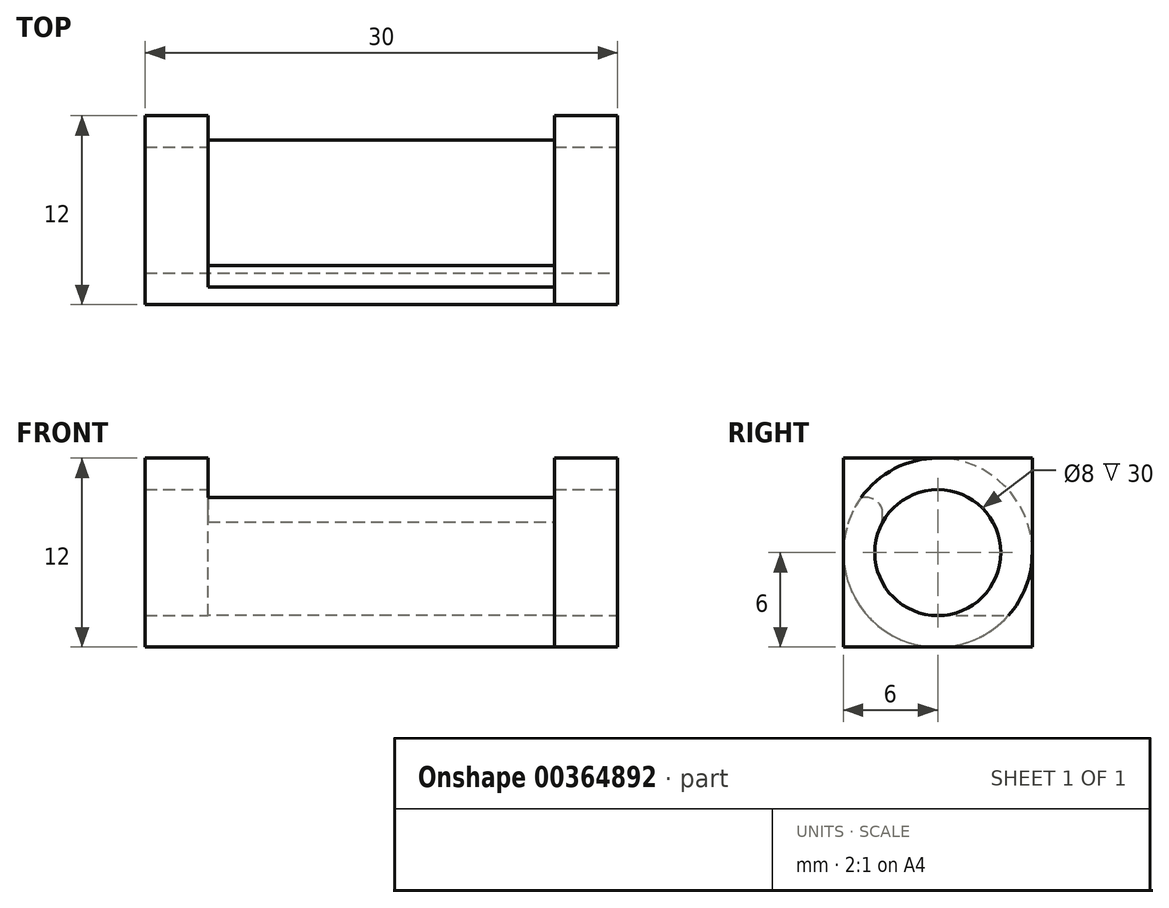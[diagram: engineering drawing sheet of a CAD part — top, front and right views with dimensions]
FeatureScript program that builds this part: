
annotation { "Feature Type Name" : "Feature", "Feature Type Description" : "" }
export const myFeature = defineFeature(function(context is Context, id is Id, definition is map)
    precondition{}
    {
        {
            var Q0;
            Q0=qCreatedBy(makeId("Right.planeOp"),FACE);
            var sketch = newSketch(context, id + "F0", { "sketchPlane" : qUnion([Q0])});
            skCircle(sketch, "E0", {"center": v(0, 0) * mm, "radius": 6 * mm});
            skSolve(sketch);
        }
        {
            var Q0;
            Q0 = qSketchRegion(id + "F0", true);
            extrude(context, id + "F1", {"entities" : qUnion([Q0]), "depth" : 30 * mm});
        }
        {
            var Q0;
            Q0=makeQuery(id+"F1.opExtrude","CAP_FACE",FACE,{"disambiguationData":[OSD([sQuery(id+"F0.wireOp",EDGE,"E0")])],"isStart":false});
            var sketch = newSketch(context, id + "F2", { "sketchPlane" : qUnion([Q0])});
            skCircle(sketch, "E1", {"center": v(0, 0) * mm, "radius": 4 * mm});
            skSolve(sketch);
        }
        {
            var Q0;
            Q0 = qSketchRegion(id + "F2", true);
            extrude(context, id + "F3", {"entities" : qUnion([Q0]), "operationType" : NewBodyOperationType.REMOVE, "endBound" : BoundingType.THROUGH_ALL, "oppositeDirection" : true, "depth" : 25 * mm});
        }
        {
            var Q0;
            Q0=makeQuery(id+"F1.opExtrude","CAP_FACE",FACE,{"disambiguationData":[OSD([sQuery(id+"F0.wireOp",EDGE,"E0")])],"isStart":false});
            cPlane(context, id + "F4", {"entities" : qUnion([Q0]), "cplaneType" : CPlaneType.OFFSET, "offset" : 4 * mm, "oppositeDirection" : true, "width" : 150 * mm, "height" : 150 * mm});
        }
        {
            var Q0;
            Q0=qCreatedBy(id+"F4.planeOp",FACE);
            var sketch = newSketch(context, id + "F5", { "sketchPlane" : qUnion([Q0])});
            skLineSegment(sketch, "E2", {"start": v(0, -4) * mm, "end": v(8, -4) * mm});
            skLineSegment(sketch, "E3", {"start": v(-4.5, 3.5) * mm, "end": v(-7.72, 3.5) * mm});
            skLineSegment(sketch, "E4", {"start": v(-7.72, 3.5) * mm, "end": v(-7.72, 9.46) * mm});
            skLineSegment(sketch, "E5", {"start": v(-7.72, 9.46) * mm, "end": v(8.98, 9.46) * mm});
            skLineSegment(sketch, "E6", {"start": v(8.98, 9.46) * mm, "end": v(8, -4) * mm});
            skLineSegment(sketch, "E7", {"start": v(0, -4) * mm, "end": v(0, 0) * mm});
            skLineSegment(sketch, "E8", {"start": v(0, 0) * mm, "end": v(-3.5, 0) * mm});
            skLineSegment(sketch, "E9", {"start": v(-3.5, 0) * mm, "end": v(-3.5, 2.5) * mm});
            skPoint(sketch, "E10.visualSharp", {"position": v(-3.5, 3.5) * mm});
            skArc(sketch, "E10.filletArc", {"start": v(-3.5, 2.5) * mm, "mid": v(-3.8, 3.2) * mm, "end": v(-4.5, 3.5) * mm});
            skSolve(sketch);
        }
        {
            var Q0;
            Q0 = qSketchRegion(id + "F5", true);
            extrude(context, id + "F6", {"entities" : qUnion([Q0]), "operationType" : NewBodyOperationType.REMOVE, "oppositeDirection" : true, "depth" : 22 * mm});
        }
        {
            var Q0;
            Q0=makeQuery(id+"F1.opExtrude","CAP_FACE",FACE,{"disambiguationData":[OSD([sQuery(id+"F0.wireOp",EDGE,"E0")])],"isStart":false});
            var sketch = newSketch(context, id + "F7", { "sketchPlane" : qUnion([Q0])});
            skLineSegment(sketch, "E11.bottom", {"start": v(6, -6) * mm, "end": v(-6, -6) * mm});
            skLineSegment(sketch, "E11.top", {"start": v(6, 6) * mm, "end": v(-6, 6) * mm});
            skLineSegment(sketch, "E11.left", {"start": v(6, -6) * mm, "end": v(6, 6) * mm});
            skLineSegment(sketch, "E11.right", {"start": v(-6, -6) * mm, "end": v(-6, 6) * mm});
            skPoint(sketch, "E11.middle", {"position": v(0, 0) * mm});
            skCircle(sketch, "E12", {"center": v(0, 0) * mm, "radius": 4 * mm});
            skSolve(sketch);
        }
        {
            var Q0;
            Q0=makeQuery(id+"F7.imprint","IMPRINT",FACE,{"disambiguationData":[TD([[makeQuery(id+"F7.imprint","IMPRINT",EDGE,{"derivedFrom":sQuery(id+"F7.wireOp",EDGE,"E12")}),-1.0]])]});
            var Q1;
            Q1=makeQuery(id+"F1.opExtrude","CAP_FACE",FACE,{"disambiguationData":[OSD([sQuery(id+"F0.wireOp",EDGE,"E0")])],"isStart":true});
            cPlane(context, id + "F8", {"entities" : qUnion([Q0, Q1]), "cplaneType" : CPlaneType.MID_PLANE, "offset" : 25 * mm, "width" : 150 * mm, "height" : 150 * mm});
        }
        {
            var Q0;
            Q0 = qSketchRegion(id + "F7", true);
            extrude(context, id + "F9", {"entities" : qUnion([Q0]), "operationType" : NewBodyOperationType.ADD, "oppositeDirection" : true, "depth" : 4 * mm});
        }
    });
